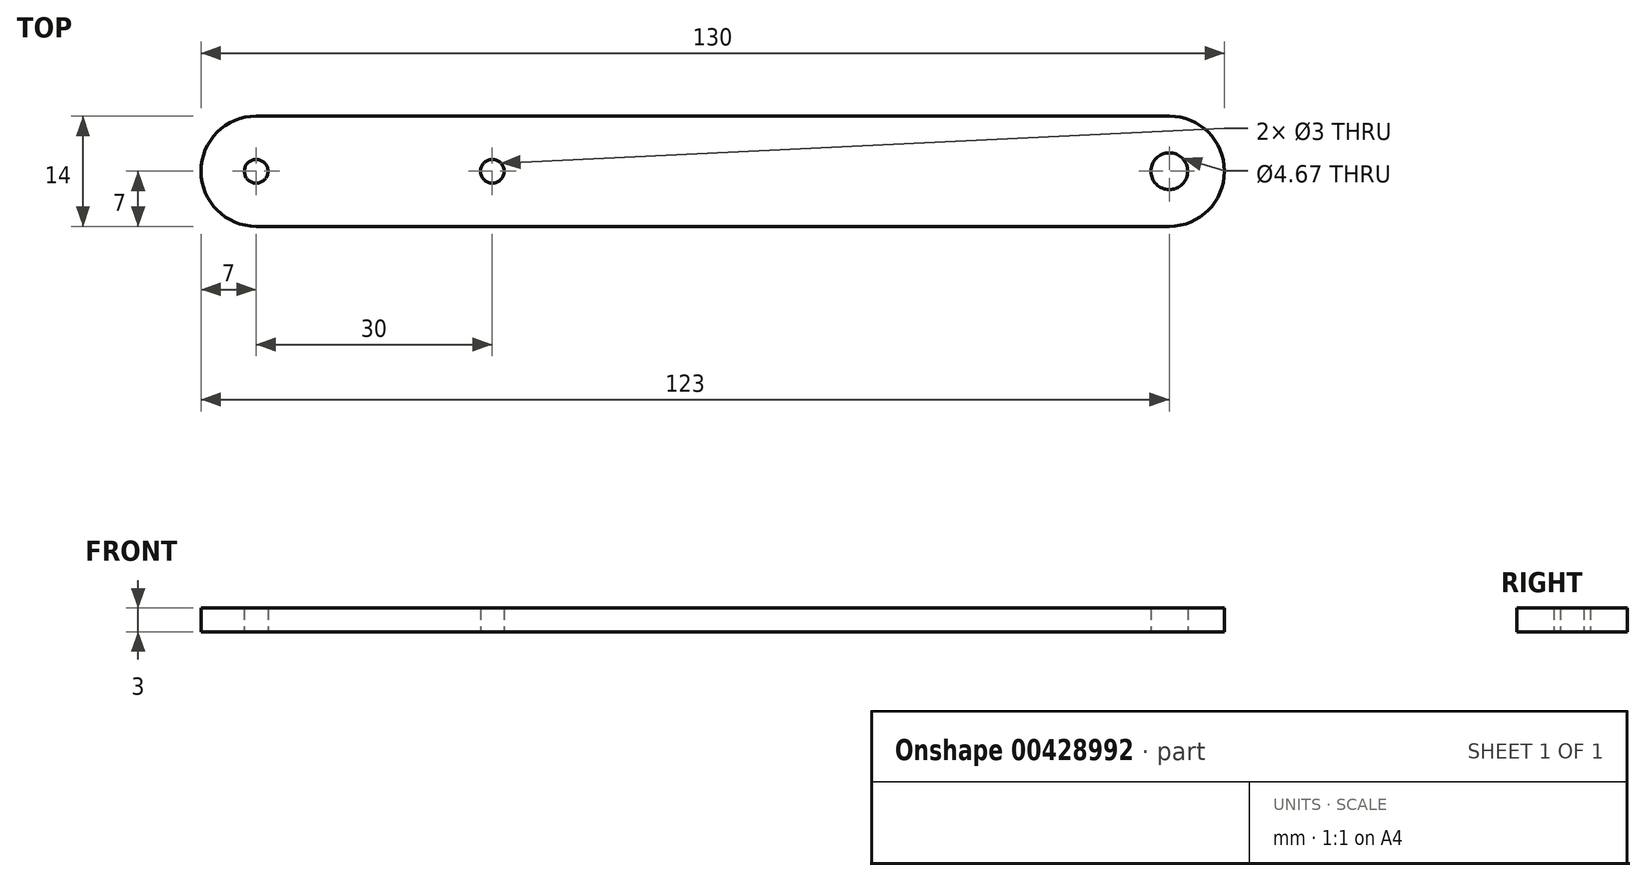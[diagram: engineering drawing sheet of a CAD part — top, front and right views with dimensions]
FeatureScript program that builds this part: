
annotation { "Feature Type Name" : "Feature", "Feature Type Description" : "" }
export const myFeature = defineFeature(function(context is Context, id is Id, definition is map)
    precondition{}
    {
        {
            var Q0;
            Q0=qCreatedBy(makeId("Top.planeOp"),FACE);
            var sketch = newSketch(context, id + "F0", { "sketchPlane" : qUnion([Q0])});
            skLineSegment(sketch, "E0.bottom", {"start": v(-58, -7) * mm, "end": v(58, -7) * mm});
            skLineSegment(sketch, "E0.top", {"start": v(-58, 7) * mm, "end": v(58, 7) * mm});
            skLineSegment(sketch, "E0.left", {"start": v(-65, 0) * mm, "end": v(-65, 0) * mm});
            skLineSegment(sketch, "E0.right", {"start": v(65, 0) * mm, "end": v(65, 0) * mm});
            skPoint(sketch, "E0.middle", {"position": v(0, 0) * mm});
            skPoint(sketch, "E1.visualSharp", {"position": v(-65, 7) * mm});
            skArc(sketch, "E1.filletArc", {"start": v(-58, 7) * mm, "mid": v(-62.95, 4.95) * mm, "end": v(-65, 0) * mm});
            skPoint(sketch, "E2.visualSharp", {"position": v(-65, -7) * mm});
            skArc(sketch, "E2.filletArc", {"start": v(-65, 0) * mm, "mid": v(-62.95, -4.95) * mm, "end": v(-58, -7) * mm});
            skPoint(sketch, "E3.visualSharp", {"position": v(65, 7) * mm});
            skArc(sketch, "E3.filletArc", {"start": v(65, 0) * mm, "mid": v(62.95, 4.95) * mm, "end": v(58, 7) * mm});
            skPoint(sketch, "E4.visualSharp", {"position": v(65, -7) * mm});
            skArc(sketch, "E4.filletArc", {"start": v(58, -7) * mm, "mid": v(62.95, -4.95) * mm, "end": v(65, 0) * mm});
            skCircle(sketch, "E5", {"center": v(58, 0) * mm, "radius": 2.33 * mm});
            skCircle(sketch, "E6", {"center": v(-58, 0) * mm, "radius": 1.5 * mm});
            skCircle(sketch, "E7", {"center": v(-28, 0) * mm, "radius": 1.5 * mm});
            skSolve(sketch);
        }
        {
            var Q0;
            Q0 = qSketchRegion(id + "F0", true);
            extrude(context, id + "F1", {"entities" : qUnion([Q0]), "depth" : 3 * mm});
        }
    });
